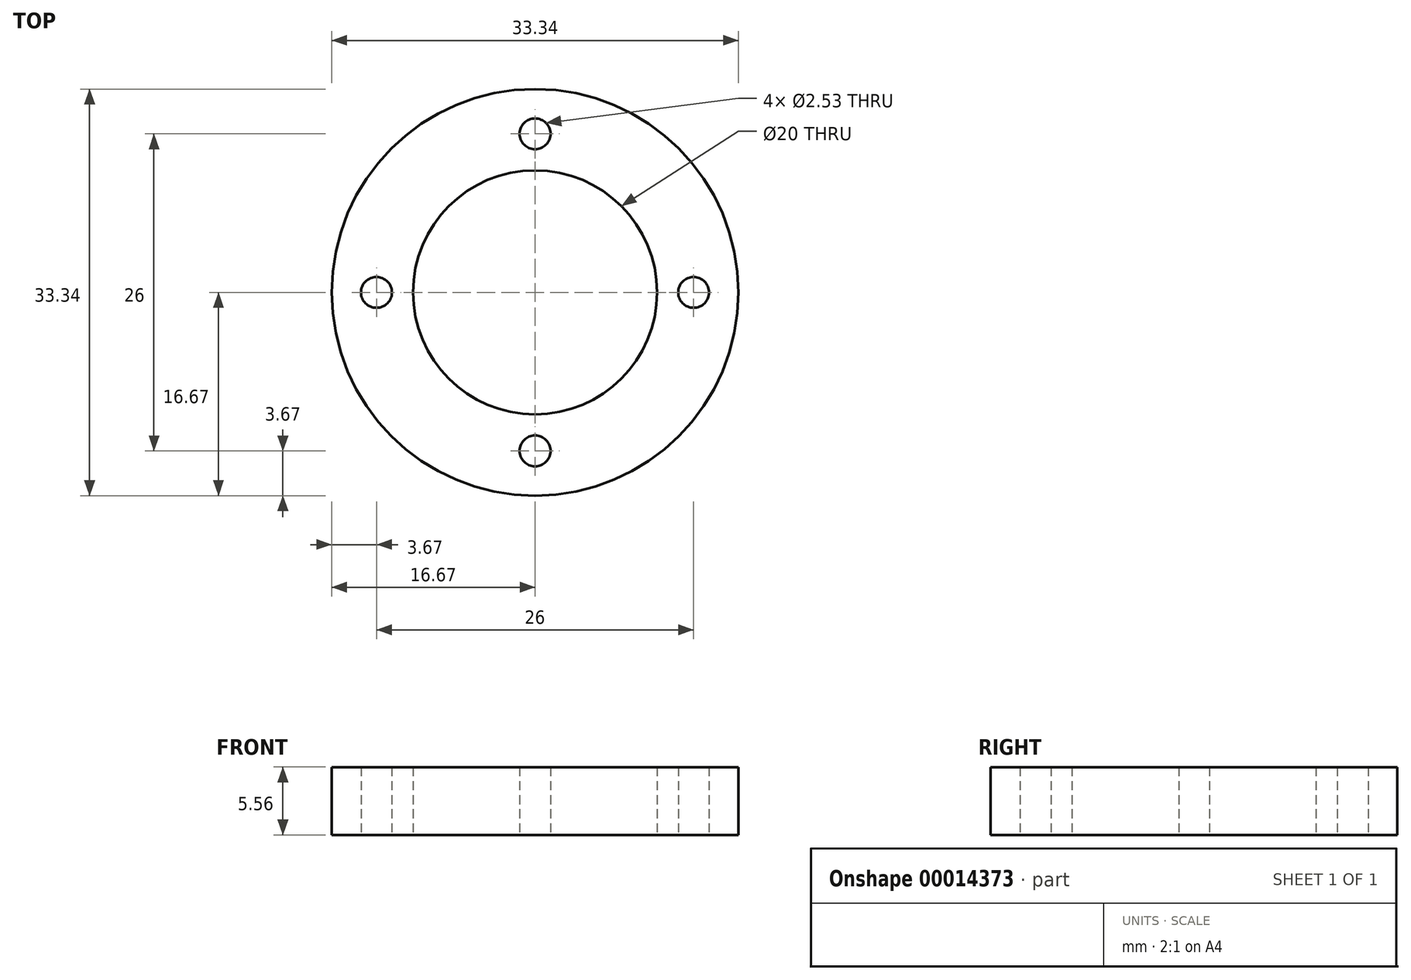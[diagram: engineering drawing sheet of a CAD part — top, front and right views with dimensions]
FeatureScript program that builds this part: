
annotation { "Feature Type Name" : "Feature", "Feature Type Description" : "" }
export const myFeature = defineFeature(function(context is Context, id is Id, definition is map)
    precondition{}
    {
        {
            var Q0;
            Q0=qCreatedBy(makeId("Top.planeOp"),FACE);
            var sketch = newSketch(context, id + "F0", { "sketchPlane" : qUnion([Q0])});
            skCircle(sketch, "E0", {"center": v(0, 0) * mm, "radius": 16.67 * mm});
            skCircle(sketch, "E1", {"center": v(0, 0) * mm, "radius": 10 * mm});
            skCircle(sketch, "E2", {"center": v(0, 0) * mm, "radius": 13 * mm, "construction": true});
            skCircle(sketch, "E3", {"center": v(-13, 0) * mm, "radius": 1.26 * mm});
            skCircle(sketch, "E4.1.0", {"center": v(0, -13) * mm, "radius": 1.26 * mm});
            skCircle(sketch, "E4.2.0", {"center": v(13, 0) * mm, "radius": 1.26 * mm});
            skCircle(sketch, "E4.3.0", {"center": v(0, 13) * mm, "radius": 1.26 * mm});
            skSolve(sketch);
        }
        {
            var Q0;
            Q0=qSketchRegion(id+"F0",true);
            extrude(context, id + "F1", {"entities" : qUnion([Q0]), "depth" : 5.56 * mm});
        }
    });
